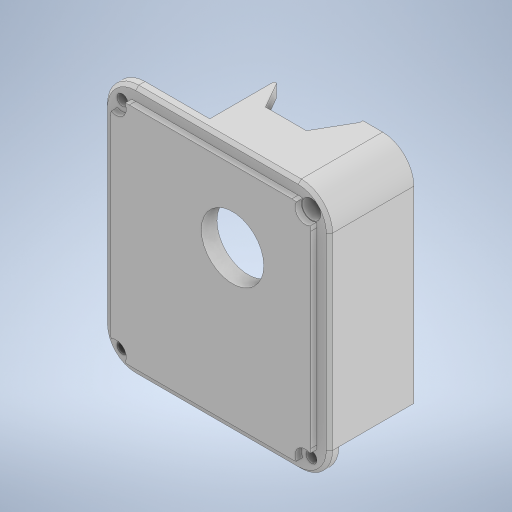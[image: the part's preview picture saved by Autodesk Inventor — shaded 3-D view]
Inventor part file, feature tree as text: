
AUTODESK INVENTOR PART (.ipt)
format: ipt  version: 2023 (Build 270158000, 158)  size: 362,496 bytes
history: native  units: mm
features: extrude x8, sketch x6, fillet x2, other x1, chamfer x1, projected_geometry x1
ambient origin geometry x8: Origin, YZ Plane, XZ Plane, XY Plane, X Axis, Y Axis, Z Axis, Center Point
bodies: Body1 (feature_tree)
feature tree (19):
  other  "솔리드1"
  sketch  "스케치1"
  extrude  "돌출1"  Depth=72.0mm
  extrude  "돌출2"  Depth=80.2mm
  extrude  "돌출3"  Depth=10.0mm
  extrude  "돌출4"  Depth=4.0mm
  extrude  "돌출5"  Depth=3.5mm
  fillet  "모깎기1"  Radius=6.5mm
  extrude  "돌출6"  Depth=3.0mm TaperAngle=0.0deg
  extrude  "돌출7"  Depth=41.3mm
  fillet  "모깎기2"  Radius=2.0mm
  extrude  "돌출8"  Depth=10.0mm
  chamfer  "모따기1"  Distance=27.0mm
  sketch  "스케치2"
  sketch  "스케치3"
  sketch  "스케치4"
  projected_geometry  "투영된 루프1"
  sketch  "스케치5"
  sketch  "스케치6"
